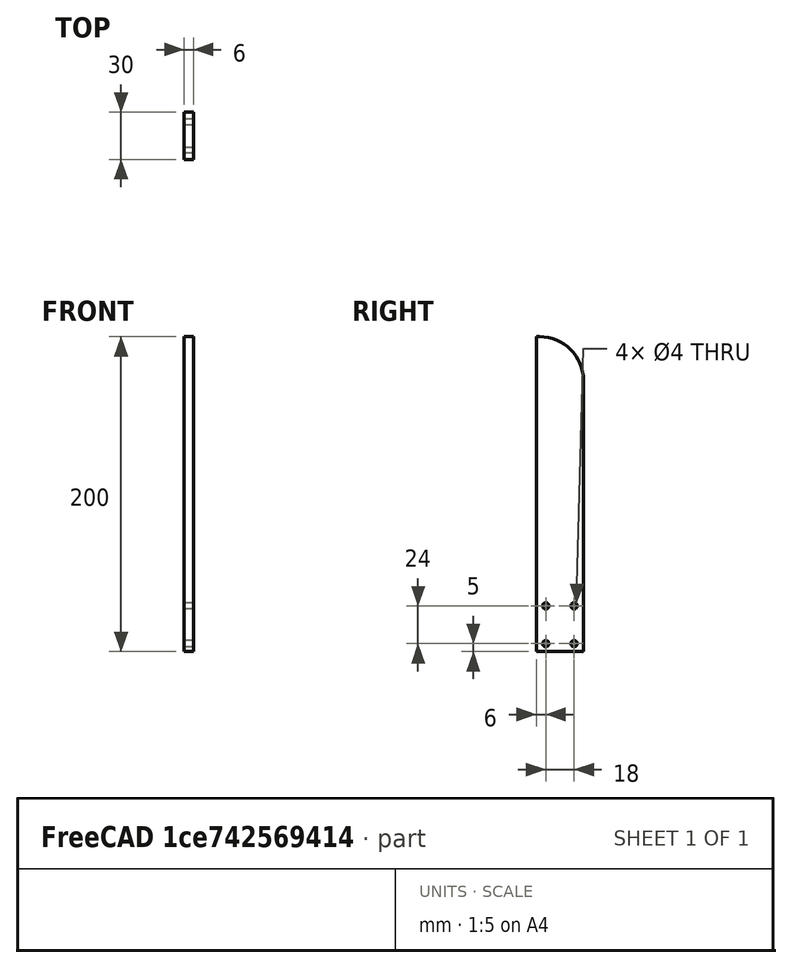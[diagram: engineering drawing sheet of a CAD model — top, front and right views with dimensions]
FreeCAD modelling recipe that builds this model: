
FCSTD DOCUMENT  (FreeCAD 0.18R4 (GitTag))
Label: Pusher2
License: All rights reserved
LicenseURL: http://en.wikipedia.org/wiki/All_rights_reserved
objects: Sketcher::SketchObject×1, PartDesign::Pad×1, PartDesign::Body×1
note: 4 computed .brp shape members not serialized (recipe doc carries the construction recipe); baked Part::Feature solids carry a one-line shape summary decoded from their .brp

FEATURE [Sketcher::SketchObject] Sketch
  MapMode = 5
  Placement = pos=(0,0,0) rot=(0.57735,0.57735,0.57735;2.0944rad)
  Support = -> [YZ_Plane]
  sketch-geometry (9):
    g0: LineSegment StartX=0 StartY=0 StartZ=0 EndX=30 EndY=0 EndZ=0
    g1: LineSegment StartX=30 StartY=0 StartZ=0 EndX=30 EndY=172 EndZ=0
    g2: LineSegment StartX=2 StartY=200 StartZ=0 EndX=0 EndY=200 EndZ=0
    g3: LineSegment StartX=0 StartY=200 StartZ=0 EndX=0 EndY=0 EndZ=0
    g4: Circle CenterX=6 CenterY=29 CenterZ=0 NormalX=0 NormalY=0 NormalZ=1 AngleXU=0 Radius=2
    g5: Circle CenterX=24 CenterY=29 CenterZ=0 NormalX=0 NormalY=0 NormalZ=1 AngleXU=0 Radius=2
    g6: Circle CenterX=6 CenterY=5 CenterZ=0 NormalX=0 NormalY=0 NormalZ=1 AngleXU=0 Radius=2
    g7: Circle CenterX=24 CenterY=5 CenterZ=0 NormalX=0 NormalY=0 NormalZ=1 AngleXU=0 Radius=2
    g8: ArcOfCircle CenterX=2 CenterY=172 CenterZ=0 NormalX=0 NormalY=0 NormalZ=1 AngleXU=0 Radius=28 StartAngle=2e-16 EndAngle=1.5708
  constraints (25):
    c: Coincident(g0,g1)
    c: Coincident(g2,g3)
    c: Coincident(g3,g0)
    c: Horizontal(g0)
    c: Horizontal(g2)
    c: Vertical(g1)
    c: Vertical(g3)
    c: DistanceX(g0,g0) = 30
    c: Coincident(g0,g-1)
    c: DistanceY(g3,g3) = 200
    c: Radius(g7) = 2
    c: Equal(g7,g5)
    c: Equal(g7,g4)
    c: Equal(g7,g6)
    c: DistanceY(g6,g7) = 0
    c: DistanceY(g4,g5) = 0
    c: DistanceY(g6,g4) = 24
    c: DistanceX(g6,g7) = 18
    c: DistanceX(g6,g4) = 0
    c: DistanceX(g5,g7) = 0
    c: Distance(g6,g3) = 6
    c: Distance(g6,g0) = 5
    c: Tangent(g2,g8) = -1.5708
    c: Tangent(g1,g8) = -1.5708
    c: Radius(g8) = 28
FEATURE [PartDesign::Pad] Pad
  Length = 6
  Length2 = 100
  Placement = pos=(0,0,0) rot=(0.57735,0.57735,0.57735;2.0944rad)
  Profile = -> Sketch
  Type = 0
FEATURE [PartDesign::Body] Body
  Group = -> [Sketch,Pad]
  Origin = -> Origin
  Tip = -> Pad
